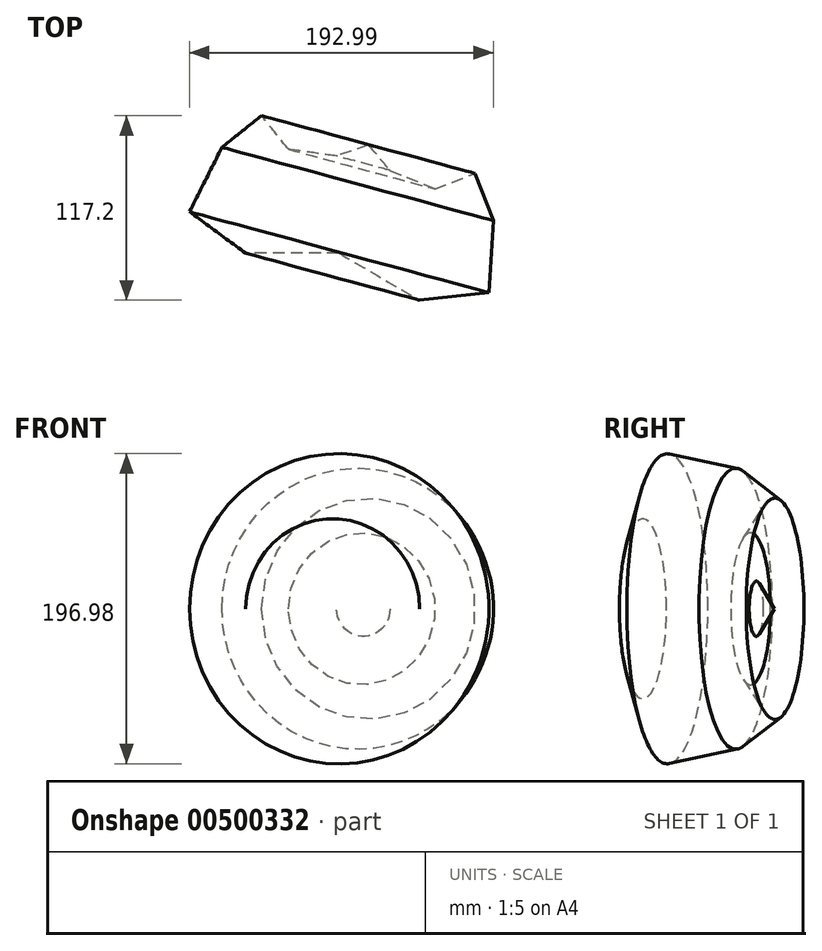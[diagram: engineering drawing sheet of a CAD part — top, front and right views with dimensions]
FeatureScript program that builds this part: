
annotation { "Feature Type Name" : "Feature", "Feature Type Description" : "" }
export const myFeature = defineFeature(function(context is Context, id is Id, definition is map)
    precondition{}
    {
        {
            var Q0;
            Q0=qCreatedBy(makeId("Top.planeOp"),FACE);
            var sketch = newSketch(context, id + "F0", { "sketchPlane" : qUnion([Q0])});
            skLineSegment(sketch, "E0", {"start": v(-49.02, 40.95) * mm, "end": v(-23.9, 61.03) * mm});
            skLineSegment(sketch, "E1", {"start": v(-23.9, 61.03) * mm, "end": v(-6.86, 39.72) * mm});
            skLineSegment(sketch, "E2", {"start": v(-6.86, 39.72) * mm, "end": v(23.8, 35.43) * mm});
            skLineSegment(sketch, "E3", {"start": v(23.8, 35.43) * mm, "end": v(43.88, 42.46) * mm});
            skLineSegment(sketch, "E4", {"start": v(43.88, 42.46) * mm, "end": v(25.3, -26.34) * mm});
            skLineSegment(sketch, "E5", {"start": v(25.3, -26.34) * mm, "end": v(-33.95, -26.34) * mm});
            skLineSegment(sketch, "E6", {"start": v(-33.95, -26.34) * mm, "end": v(-69.6, 0) * mm});
            skLineSegment(sketch, "E7", {"start": v(-69.6, 0) * mm, "end": v(-49.02, 40.95) * mm});
            skSolve(sketch);
        }
        {
            var Q0;
            Q0=makeQuery(id+"F0.imprint","IMPRINT",FACE,{"disambiguationData":[TD([[makeQuery(id+"F0.imprint","IMPRINT",EDGE,{"derivedFrom":sQuery(id+"F0.wireOp",EDGE,"E0")}),-1.0]])]});
            var Q1;
            Q1=sQuery(id+"F0.wireOp",EDGE,"E4");
            revolve(context, id + "F1", {"entities" : qUnion([Q0]), "axis" : qUnion([Q1]), "revolveType" : RevolveType.FULL});
        }
    });
